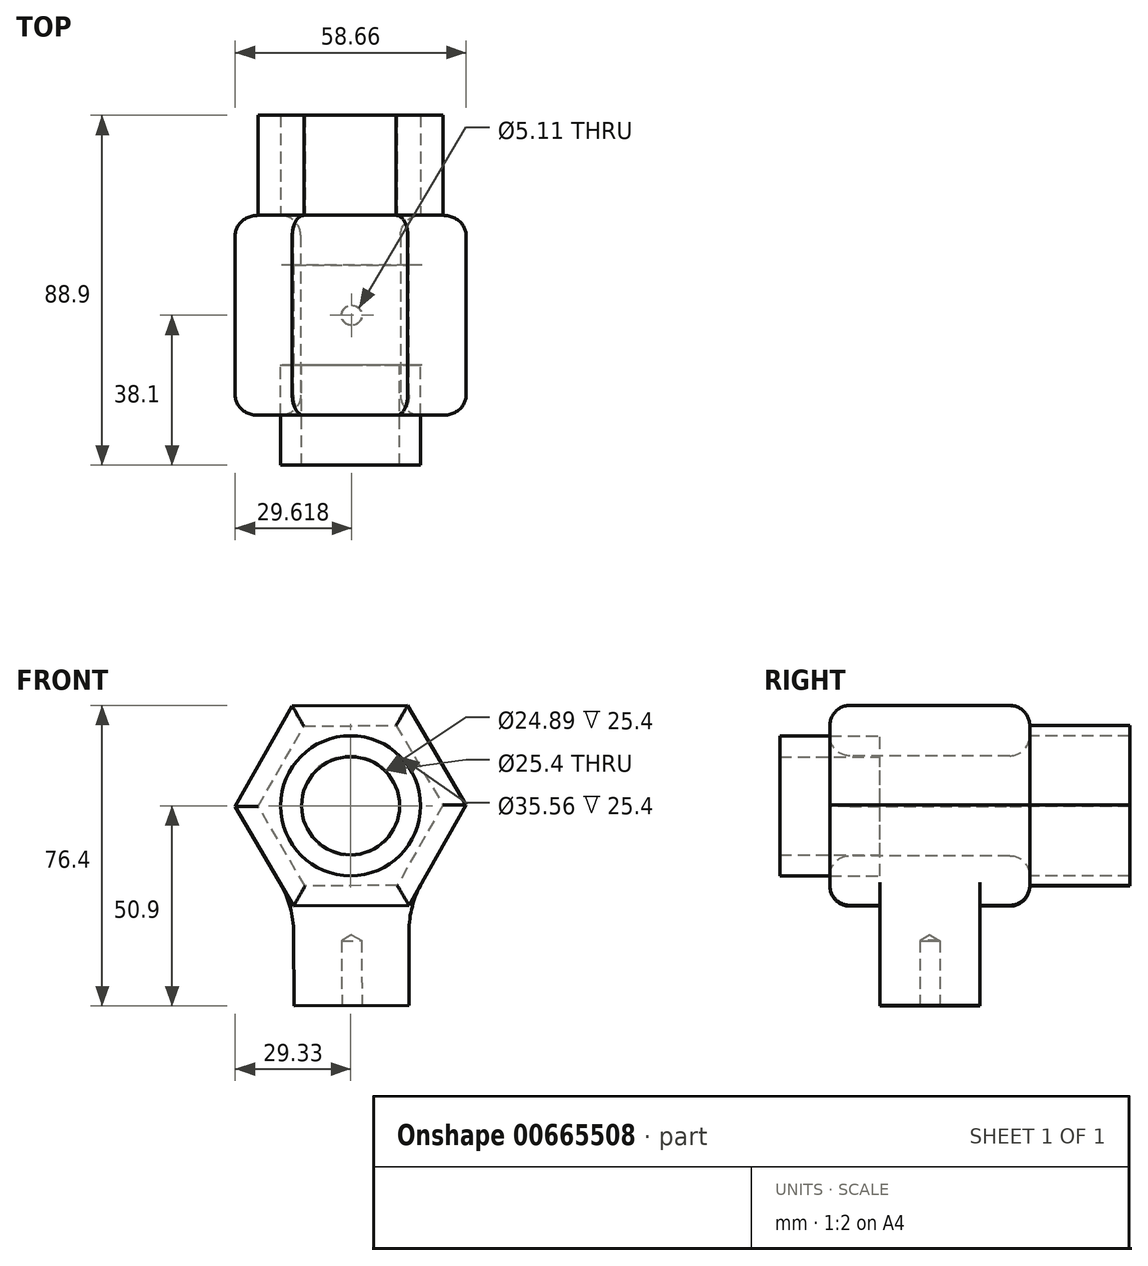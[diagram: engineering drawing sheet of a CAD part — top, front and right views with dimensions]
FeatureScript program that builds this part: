
annotation { "Feature Type Name" : "Feature", "Feature Type Description" : "" }
export const myFeature = defineFeature(function(context is Context, id is Id, definition is map)
    precondition{}
    {
        {
            var Q0;
            Q0=qCreatedBy(makeId("Front.planeOp"),FACE);
            var sketch = newSketch(context, id + "F0", { "sketchPlane" : qUnion([Q0])});
            skCircle(sketch, "E0.cCircle", {"center": v(0, 0) * mm, "radius": 25.4 * mm, "construction": true});
            skLineSegment(sketch, "E0.0", {"start": v(29.33, 0.2) * mm, "end": v(14.84, -25.3) * mm});
            skLineSegment(sketch, "E0.1", {"start": v(14.84, -25.3) * mm, "end": v(-14.5, -25.5) * mm});
            skLineSegment(sketch, "E0.2", {"start": v(-14.5, -25.5) * mm, "end": v(-29.33, -0.2) * mm});
            skLineSegment(sketch, "E0.3", {"start": v(-29.33, -0.2) * mm, "end": v(-14.84, 25.3) * mm});
            skLineSegment(sketch, "E0.4", {"start": v(-14.84, 25.3) * mm, "end": v(14.5, 25.5) * mm});
            skLineSegment(sketch, "E0.5", {"start": v(14.5, 25.5) * mm, "end": v(29.33, 0.2) * mm});
            skPoint(sketch, "E0.0.midPoint", {"position": v(22.08, -12.55) * mm});
            skLineSegment(sketch, "E1", {"start": v(-14.5, -25.5) * mm, "end": v(-14.32, -50.9) * mm});
            skLineSegment(sketch, "E2", {"start": v(-14.32, -50.9) * mm, "end": v(14.84, -50.7) * mm});
            skLineSegment(sketch, "E3", {"start": v(14.84, -25.3) * mm, "end": v(14.84, -50.7) * mm});
            skSolve(sketch);
        }
        {
            var Q0;
            Q0=makeQuery(id+"F0.imprint","IMPRINT",FACE,{"disambiguationData":[TD([[makeQuery(id+"F0.imprint","IMPRINT",EDGE,{"derivedFrom":sQuery(id+"F0.wireOp",EDGE,"E0.0")}),-1.0]])]});
            extrude(context, id + "F1", {"entities" : qUnion([Q0]), "depth" : 50.8 * mm, "offsetDistance" : 25.4 * mm, "symmetric" : true});
        }
        {
            var Q0;
            Q0=makeQuery(id+"F0.imprint","IMPRINT",FACE,{"disambiguationData":[TD([[makeQuery(id+"F0.imprint","IMPRINT",EDGE,{"derivedFrom":sQuery(id+"F0.wireOp",EDGE,"E0.1")}),1.0]])]});
            extrude(context, id + "F2", {"entities" : qUnion([Q0]), "operationType" : NewBodyOperationType.ADD, "depth" : 25.4 * mm, "offsetDistance" : 25.4 * mm, "symmetric" : true});
        }
        {
            var Q0;
            {var subQ0=sQuery(id+"F0.wireOp",EDGE,"E3");var subQ1=sQuery(id+"F0.wireOp",EDGE,"E0.1");var subQ2=sQuery(id+"F0.wireOp",EDGE,"E0.0");Q0=makeQuery(id+"F2.boolean.opBoolean","MERGE",EDGE,{"derivedFrom":[makeQuery(id+"F1.opExtrude","SWEPT_EDGE",EDGE,{"disambiguationData":[OSD([subQ2,subQ1,subQ0])]}),makeQuery(id+"F2.opExtrude","SWEPT_EDGE",EDGE,{"disambiguationData":[OSD([subQ2,subQ1,subQ0])]})]});}
            var Q1;
            {var subQ0=sQuery(id+"F0.wireOp",EDGE,"E1");var subQ1=sQuery(id+"F0.wireOp",EDGE,"E0.2");var subQ2=sQuery(id+"F0.wireOp",EDGE,"E0.1");Q1=makeQuery(id+"F2.boolean.opBoolean","MERGE",EDGE,{"derivedFrom":[makeQuery(id+"F1.opExtrude","SWEPT_EDGE",EDGE,{"disambiguationData":[OSD([subQ2,subQ1,subQ0])]}),makeQuery(id+"F2.opExtrude","SWEPT_EDGE",EDGE,{"disambiguationData":[OSD([subQ2,subQ1,subQ0])]})]});}
            fillet(context, id + "F3", {"entities" : qUnion([Q0, Q1]), "radius" : 25.4 * mm, "tangentPropagation" : true, "allowEdgeOverflow" : false});
        }
        {
            var Q0;
            Q0=makeQuery(id+"F1.opExtrude","CAP_FACE",FACE,{"disambiguationData":[OSD([sQuery(id+"F0.wireOp",EDGE,"E0.0"),sQuery(id+"F0.wireOp",EDGE,"E0.1"),sQuery(id+"F0.wireOp",EDGE,"E0.2"),sQuery(id+"F0.wireOp",EDGE,"E0.3"),sQuery(id+"F0.wireOp",EDGE,"E0.4"),sQuery(id+"F0.wireOp",EDGE,"E0.5")])],"isStart":false});
            var sketch = newSketch(context, id + "F4", { "sketchPlane" : qUnion([Q0])});
            skCircle(sketch, "E4", {"center": v(0, 0) * mm, "radius": 12.7 * mm});
            skSolve(sketch);
        }
        {
            var Q0;
            Q0 = qSketchRegion(id + "F4", true);
            extrude(context, id + "F5", {"entities" : qUnion([Q0]), "operationType" : NewBodyOperationType.REMOVE, "endBound" : BoundingType.THROUGH_ALL, "oppositeDirection" : true, "depth" : 25.4 * mm, "offsetDistance" : 25.4 * mm});
        }
        {
            var Q0;
            Q0=makeQuery(id+"F1.opExtrude","CAP_FACE",FACE,{"disambiguationData":[OSD([sQuery(id+"F0.wireOp",EDGE,"E0.0"),sQuery(id+"F0.wireOp",EDGE,"E0.1"),sQuery(id+"F0.wireOp",EDGE,"E0.2"),sQuery(id+"F0.wireOp",EDGE,"E0.3"),sQuery(id+"F0.wireOp",EDGE,"E0.4"),sQuery(id+"F0.wireOp",EDGE,"E0.5")])],"isStart":false});
            var Q1;
            Q1=makeQuery(id+"F1.opExtrude","CAP_FACE",FACE,{"disambiguationData":[OSD([sQuery(id+"F0.wireOp",EDGE,"E0.0"),sQuery(id+"F0.wireOp",EDGE,"E0.1"),sQuery(id+"F0.wireOp",EDGE,"E0.2"),sQuery(id+"F0.wireOp",EDGE,"E0.3"),sQuery(id+"F0.wireOp",EDGE,"E0.4"),sQuery(id+"F0.wireOp",EDGE,"E0.5")])],"isStart":true});
            fillet(context, id + "F6", {"entities" : qUnion([Q0, Q1]), "radius" : 5.08 * mm, "tangentPropagation" : true, "allowEdgeOverflow" : false});
        }
        {
            var Q0;
            Q0=makeQuery(id+"F2.opExtrude","SWEPT_FACE",FACE,{"disambiguationData":[OSD([sQuery(id+"F0.wireOp",EDGE,"E2")])]});
            var sketch = newSketch(context, id + "F7", { "sketchPlane" : qUnion([Q0])});
            skPoint(sketch, "E5", {"position": v(0, 0) * mm});
            skSolve(sketch);
        }
        {
            var Q0;
            Q0=sQuery(id+"F7.wireOp",VERTEX,"E5");
            var Q1;
            Q1=makeQuery(id+"F1.opExtrude","SWEPT_BODY",BODY,{"disambiguationData":[OSD([sQuery(id+"F0.wireOp",EDGE,"E0.0"),sQuery(id+"F0.wireOp",EDGE,"E0.1"),sQuery(id+"F0.wireOp",EDGE,"E0.2"),sQuery(id+"F0.wireOp",EDGE,"E0.3"),sQuery(id+"F0.wireOp",EDGE,"E0.4"),sQuery(id+"F0.wireOp",EDGE,"E0.5")])]});
            hole(context, id + "F8", {"style" : HoleStyle.SIMPLE, "endStyle" : HoleEndStyle.BLIND, "standardTappedOrClearance" : lookupTablePath({ "standard" : "ANSI", "engagement" : "75%", "pitch" : "20 tpi", "size" : "1/4", "type" : "Tapped" }), "standardBlindInLast" : lookupTablePath({ "standard" : "ANSI", "engagement" : "75%", "pitch" : "20 tpi", "size" : "1/4", "type" : "Tapped" }), "holeDiameter" : 5.1 * mm, "majorDiameter" : 6.35 * mm, "showTappedDepth" : true, "holeDepth" : 16.51 * mm, "tappedDepth" : 12.7 * mm, "tapClearance" : 3, "startFromSketch" : true, "locations" : qUnion([Q0]), "scope" : qUnion([Q1])});
        }
        {
            var Q0;
            Q0=makeQuery(id+"F1.opExtrude","CAP_FACE",FACE,{"disambiguationData":[OSD([sQuery(id+"F0.wireOp",EDGE,"E0.0"),sQuery(id+"F0.wireOp",EDGE,"E0.1"),sQuery(id+"F0.wireOp",EDGE,"E0.2"),sQuery(id+"F0.wireOp",EDGE,"E0.3"),sQuery(id+"F0.wireOp",EDGE,"E0.4"),sQuery(id+"F0.wireOp",EDGE,"E0.5")])],"isStart":true});
            var Q1;
            Q1=sQuery(id+"FWjbf9uAmLF2NNp_1.wireOp",EDGE,"0a234ff0-5dc8-44a1-b7ef-be9a88c13d54");
            extrude(context, id + "F9", {"entities" : qUnion([Q0]), "surfaceEntities" : qUnion([Q1]), "depth" : 25.4 * mm, "offsetDistance" : 25.4 * mm});
        }
        {
            var Q0;
            Q0=makeQuery(id+"F1.opExtrude","CAP_FACE",FACE,{"disambiguationData":[OSD([sQuery(id+"F0.wireOp",EDGE,"E0.0"),sQuery(id+"F0.wireOp",EDGE,"E0.1"),sQuery(id+"F0.wireOp",EDGE,"E0.2"),sQuery(id+"F0.wireOp",EDGE,"E0.3"),sQuery(id+"F0.wireOp",EDGE,"E0.4"),sQuery(id+"F0.wireOp",EDGE,"E0.5")])],"isStart":false});
            var sketch = newSketch(context, id + "F10", { "sketchPlane" : qUnion([Q0])});
            skCircle(sketch, "E6.0", {"center": v(0, 0) * mm, "radius": 12.45 * mm});
            skSolve(sketch);
        }
        {
            var Q0;
            Q0=makeQuery(id+"F10.imprint","IMPRINT",FACE,{"disambiguationData":[TD([[makeQuery(id+"F10.imprint","IMPRINT",EDGE,{"derivedFrom":sQuery(id+"F10.wireOp",EDGE,"E6.0")}),-1.0]])]});
            var Q1;
            Q1=sQuery(id+"F10.wireOp",EDGE,"E6.0");
            extrude(context, id + "F11", {"entities" : qUnion([Q0]), "surfaceEntities" : qUnion([Q1]), "depth" : 25.4 * mm, "offsetDistance" : 25.4 * mm, "symmetric" : true});
        }
    });
